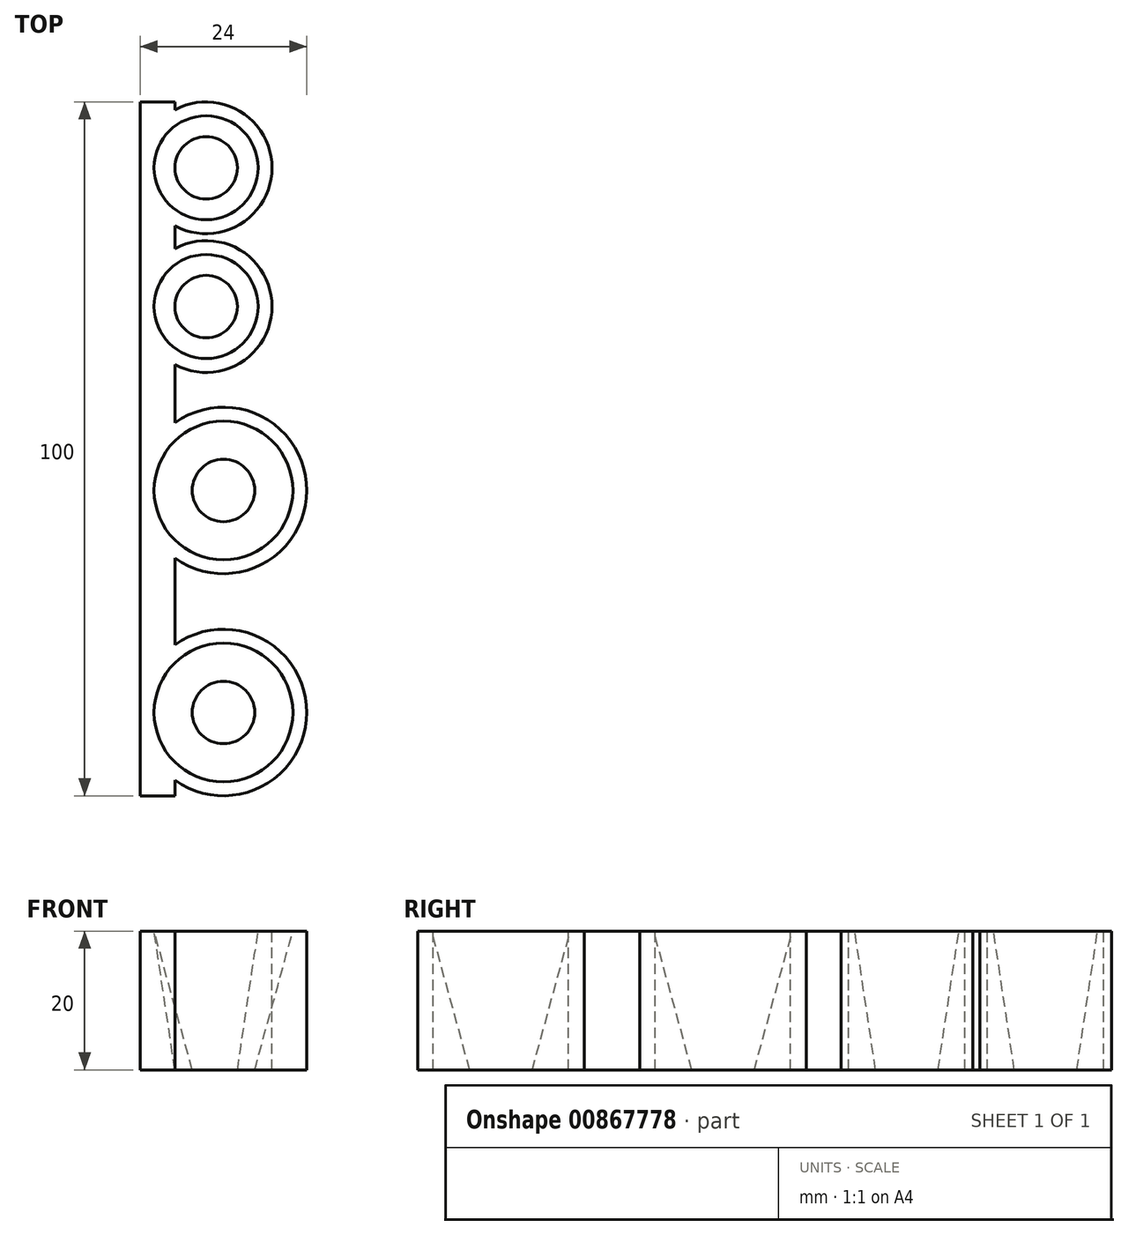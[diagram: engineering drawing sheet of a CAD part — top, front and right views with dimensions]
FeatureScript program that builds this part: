
annotation { "Feature Type Name" : "Feature", "Feature Type Description" : "" }
export const myFeature = defineFeature(function(context is Context, id is Id, definition is map)
    precondition{}
    {
        {
            var Q0;
            Q0=qCreatedBy(makeId("Right.planeOp"),FACE);
            var sketch = newSketch(context, id + "F0", { "sketchPlane" : qUnion([Q0])});
            skLineSegment(sketch, "E0.bottom", {"start": v(50, -10) * mm, "end": v(-50, -10) * mm});
            skLineSegment(sketch, "E0.top", {"start": v(50, 10) * mm, "end": v(-50, 10) * mm});
            skLineSegment(sketch, "E0.left", {"start": v(50, -10) * mm, "end": v(50, 10) * mm});
            skLineSegment(sketch, "E0.right", {"start": v(-50, -10) * mm, "end": v(-50, 10) * mm});
            skPoint(sketch, "E0.middle", {"position": v(0, 0) * mm});
            skSolve(sketch);
        }
        {
            var Q0;
            Q0=makeQuery(id+"F0.imprint","IMPRINT",FACE,{"disambiguationData":[TD([[makeQuery(id+"F0.imprint","IMPRINT",EDGE,{"derivedFrom":sQuery(id+"F0.wireOp",EDGE,"E0.bottom")}),-1.0]])]});
            extrude(context, id + "F1", {"entities" : qUnion([Q0]), "endBound" : BoundingType.SYMMETRIC, "depth" : 25 * mm, "offsetDistance" : 25 * mm});
        }
        {
            var Q0;
            Q0=makeQuery(id+"F1.opExtrude","SWEPT_FACE",FACE,{"disambiguationData":[OSD([sQuery(id+"F0.wireOp",EDGE,"E0.top")])]});
            var sketch = newSketch(context, id + "F2", { "sketchPlane" : qUnion([Q0])});
            skLineSegment(sketch, "E1", {"start": v(-12.5, -50) * mm, "end": v(11.5, -50) * mm});
            skCircle(sketch, "E2", {"center": v(-0.5, -38) * mm, "radius": 12 * mm});
            skPoint(sketch, "E2.centerSnap0", {"position": v(-0.5, -50) * mm});
            skCircle(sketch, "E3", {"center": v(-0.5, -6) * mm, "radius": 10 * mm});
            skCircle(sketch, "E4", {"center": v(-0.5, -38) * mm, "radius": 10 * mm});
            skCircle(sketch, "E5", {"center": v(-0.5, -6) * mm, "radius": 12 * mm});
            skLineSegment(sketch, "E6", {"start": v(-12.5, 50) * mm, "end": v(-3, 50) * mm});
            skCircle(sketch, "E7", {"center": v(-3, 40.5) * mm, "radius": 9.5 * mm});
            skCircle(sketch, "E8", {"center": v(-3, 40.5) * mm, "radius": 7.5 * mm});
            skCircle(sketch, "E9", {"center": v(-3, 20.5) * mm, "radius": 9.5 * mm});
            skCircle(sketch, "E10", {"center": v(-3, 20.5) * mm, "radius": 7.5 * mm});
            skLineSegment(sketch, "E11", {"start": v(-7.5, -50) * mm, "end": v(-7.5, -47.75) * mm});
            skLineSegment(sketch, "E12.trimOffspring", {"start": v(-7.5, -28.25) * mm, "end": v(-7.5, -15.75) * mm});
            skLineSegment(sketch, "E13.trimOffspring", {"start": v(-7.5, 3.75) * mm, "end": v(-7.5, 12.13) * mm});
            skLineSegment(sketch, "E14.trimOffspring", {"start": v(-7.5, 28.87) * mm, "end": v(-7.5, 32.13) * mm});
            skLineSegment(sketch, "E15.trimOffspring", {"start": v(-7.5, 48.87) * mm, "end": v(-7.5, 50) * mm});
            skSolve(sketch);
        }
        {
            var Q0;
            Q0=makeQuery(id+"F1.opExtrude","SWEPT_FACE",FACE,{"disambiguationData":[OSD([sQuery(id+"F0.wireOp",EDGE,"E0.bottom")])]});
            var sketch = newSketch(context, id + "F3", { "sketchPlane" : qUnion([Q0])});
            skLineSegment(sketch, "E16", {"start": v(-12.5, 50) * mm, "end": v(-0.5, 50) * mm});
            skCircle(sketch, "E17", {"center": v(-0.5, 38) * mm, "radius": 6.5 * mm});
            skCircle(sketch, "E18", {"center": v(-0.5, 38) * mm, "radius": 4.5 * mm});
            skCircle(sketch, "E19.0.1.0", {"center": v(-0.5, 6) * mm, "radius": 6.5 * mm});
            skCircle(sketch, "E19.0.1.1", {"center": v(-0.5, 6) * mm, "radius": 4.5 * mm});
            skLineSegment(sketch, "E19.direction1", {"start": v(-0.5, 38) * mm, "end": v(37, 38) * mm, "construction": true});
            skLineSegment(sketch, "E19.direction2", {"start": v(-0.5, 38) * mm, "end": v(-0.5, 6) * mm, "construction": true});
            skLineSegment(sketch, "E20", {"start": v(-12.5, -50) * mm, "end": v(-3, -50) * mm});
            skCircle(sketch, "E21", {"center": v(-3, -40.5) * mm, "radius": 4.5 * mm});
            skCircle(sketch, "E22", {"center": v(-3, -40.5) * mm, "radius": 6.5 * mm});
            skCircle(sketch, "E23.0.1.0", {"center": v(-3, -20.5) * mm, "radius": 6.5 * mm});
            skCircle(sketch, "E23.0.1.1", {"center": v(-3, -20.5) * mm, "radius": 4.5 * mm});
            skLineSegment(sketch, "E23.direction1", {"start": v(-3, -40.5) * mm, "end": v(34.5, -40.5) * mm, "construction": true});
            skLineSegment(sketch, "E23.direction2", {"start": v(-3, -40.5) * mm, "end": v(-3, -20.5) * mm, "construction": true});
            skLineSegment(sketch, "E24", {"start": v(-4.5, 50) * mm, "end": v(-4.5, 43.12) * mm});
            skLineSegment(sketch, "E25.trimOffspring", {"start": v(-4.5, -46.82) * mm, "end": v(-4.5, -50) * mm});
            skLineSegment(sketch, "E26.trimOffspring", {"start": v(-4.5, -26.82) * mm, "end": v(-4.5, -34.18) * mm});
            skLineSegment(sketch, "E27.trimOffspring", {"start": v(-4.5, 0.88) * mm, "end": v(-4.5, -14.18) * mm});
            skLineSegment(sketch, "E28.trimOffspring", {"start": v(-4.5, 32.88) * mm, "end": v(-4.5, 11.12) * mm});
            skSolve(sketch);
        }
        {
            var Q1;
            {var subQ0=sQuery(id+"F2.wireOp",EDGE,"E4");var subQ1=makeQuery(id+"F1.opExtrude","CAP_EDGE",EDGE,{"disambiguationData":[OSD([sQuery(id+"F0.wireOp",EDGE,"E0.top")])],"isStart":false});var subQ2=makeQuery(id+"F2.imprint","INTERSECT",VERTEX,{"disambiguationData":[OD(0.0)],"derivedFrom":[subQ1,subQ0]});Q1=makeQuery(id+"F2.imprint","IMPRINT",FACE,{"disambiguationData":[TD([[makeQuery(id+"F2.imprint","IMPRINT",EDGE,{"disambiguationData":[TD([[subQ2,-1.0]])],"derivedFrom":subQ0}),1.0]])]});}
            var Q2;
            {var subQ0=sQuery(id+"F3.wireOp",EDGE,"E18");var subQ1=makeQuery(id+"F1.opExtrude","CAP_EDGE",EDGE,{"disambiguationData":[OSD([sQuery(id+"F0.wireOp",EDGE,"E0.bottom")])],"isStart":false});var subQ2=makeQuery(id+"F3.imprint","INTERSECT",VERTEX,{"disambiguationData":[OD(0.0)],"derivedFrom":[subQ1,subQ0]});Q2=makeQuery(id+"F3.imprint","IMPRINT",FACE,{"disambiguationData":[TD([[makeQuery(id+"F3.imprint","IMPRINT",EDGE,{"disambiguationData":[TD([[subQ2,-1.0]])],"derivedFrom":subQ0}),1.0]])]});}
            loft(context, id + "F4", {"operationType" : NewBodyOperationType.REMOVE, "sheetProfilesArray" : [{ "sheetProfileEntities" : qUnion([Q1]) }, { "sheetProfileEntities" : qUnion([Q2]) }]});
        }
        {
            var Q1;
            {var subQ0=sQuery(id+"F2.wireOp",EDGE,"E3");var subQ1=makeQuery(id+"F1.opExtrude","CAP_EDGE",EDGE,{"disambiguationData":[OSD([sQuery(id+"F0.wireOp",EDGE,"E0.top")])],"isStart":false});var subQ2=makeQuery(id+"F2.imprint","INTERSECT",VERTEX,{"disambiguationData":[OD(0.0)],"derivedFrom":[subQ1,subQ0]});Q1=makeQuery(id+"F2.imprint","IMPRINT",FACE,{"disambiguationData":[TD([[makeQuery(id+"F2.imprint","IMPRINT",EDGE,{"disambiguationData":[TD([[subQ2,-1.0]])],"derivedFrom":subQ0}),1.0]])]});}
            var Q2;
            {var subQ0=sQuery(id+"F3.wireOp",EDGE,"E19.0.1.1");var subQ1=makeQuery(id+"F1.opExtrude","CAP_EDGE",EDGE,{"disambiguationData":[OSD([sQuery(id+"F0.wireOp",EDGE,"E0.bottom")])],"isStart":false});var subQ2=makeQuery(id+"F3.imprint","INTERSECT",VERTEX,{"disambiguationData":[OD(0.0)],"derivedFrom":[subQ1,subQ0]});Q2=makeQuery(id+"F3.imprint","IMPRINT",FACE,{"disambiguationData":[TD([[makeQuery(id+"F3.imprint","IMPRINT",EDGE,{"disambiguationData":[TD([[subQ2,-1.0]])],"derivedFrom":subQ0}),1.0]])]});}
            loft(context, id + "F5", {"operationType" : NewBodyOperationType.REMOVE, "sheetProfilesArray" : [{ "sheetProfileEntities" : qUnion([Q1]) }, { "sheetProfileEntities" : qUnion([Q2]) }]});
        }
        {
            var Q1;
            {var subQ0=sQuery(id+"F2.wireOp",EDGE,"E10");var subQ1=makeQuery(id+"F1.opExtrude","CAP_EDGE",EDGE,{"disambiguationData":[OSD([sQuery(id+"F0.wireOp",EDGE,"E0.top")])],"isStart":false});var subQ2=makeQuery(id+"F2.imprint","INTERSECT",VERTEX,{"disambiguationData":[OD(0.0)],"derivedFrom":[subQ1,subQ0]});Q1=makeQuery(id+"F2.imprint","IMPRINT",FACE,{"disambiguationData":[TD([[makeQuery(id+"F2.imprint","IMPRINT",EDGE,{"disambiguationData":[TD([[subQ2,-1.0]])],"derivedFrom":subQ0}),1.0]])]});}
            var Q2;
            {var subQ0=sQuery(id+"F3.wireOp",EDGE,"E23.0.1.1");var subQ1=makeQuery(id+"F1.opExtrude","CAP_EDGE",EDGE,{"disambiguationData":[OSD([sQuery(id+"F0.wireOp",EDGE,"E0.bottom")])],"isStart":false});var subQ2=makeQuery(id+"F3.imprint","INTERSECT",VERTEX,{"disambiguationData":[OD(0.0)],"derivedFrom":[subQ1,subQ0]});Q2=makeQuery(id+"F3.imprint","IMPRINT",FACE,{"disambiguationData":[TD([[makeQuery(id+"F3.imprint","IMPRINT",EDGE,{"disambiguationData":[TD([[subQ2,1.0]])],"derivedFrom":subQ0}),1.0]])]});}
            loft(context, id + "F6", {"operationType" : NewBodyOperationType.REMOVE, "sheetProfilesArray" : [{ "sheetProfileEntities" : qUnion([Q1]) }, { "sheetProfileEntities" : qUnion([Q2]) }]});
        }
        {
            var Q1;
            {var subQ0=sQuery(id+"F2.wireOp",EDGE,"E8");var subQ1=makeQuery(id+"F1.opExtrude","CAP_EDGE",EDGE,{"disambiguationData":[OSD([sQuery(id+"F0.wireOp",EDGE,"E0.top")])],"isStart":false});var subQ2=makeQuery(id+"F2.imprint","INTERSECT",VERTEX,{"disambiguationData":[OD(0.0)],"derivedFrom":[subQ1,subQ0]});Q1=makeQuery(id+"F2.imprint","IMPRINT",FACE,{"disambiguationData":[TD([[makeQuery(id+"F2.imprint","IMPRINT",EDGE,{"disambiguationData":[TD([[subQ2,1.0]])],"derivedFrom":subQ0}),1.0]])]});}
            var Q2;
            {var subQ0=sQuery(id+"F3.wireOp",EDGE,"E21");var subQ1=makeQuery(id+"F1.opExtrude","CAP_EDGE",EDGE,{"disambiguationData":[OSD([sQuery(id+"F0.wireOp",EDGE,"E0.bottom")])],"isStart":false});var subQ2=makeQuery(id+"F3.imprint","INTERSECT",VERTEX,{"disambiguationData":[OD(0.0)],"derivedFrom":[subQ1,subQ0]});Q2=makeQuery(id+"F3.imprint","IMPRINT",FACE,{"disambiguationData":[TD([[makeQuery(id+"F3.imprint","IMPRINT",EDGE,{"disambiguationData":[TD([[subQ2,1.0]])],"derivedFrom":subQ0}),1.0]])]});}
            loft(context, id + "F7", {"operationType" : NewBodyOperationType.REMOVE, "sheetProfilesArray" : [{ "sheetProfileEntities" : qUnion([Q1]) }, { "sheetProfileEntities" : qUnion([Q2]) }]});
        }
        {
            var Q0;
            {var subQ5=sQuery(id+"F2.wireOp",EDGE,"E12.trimOffspring");Q0=makeQuery(id+"F2.imprint","IMPRINT",FACE,{"disambiguationData":[TD([[makeQuery(id+"F2.imprint","IMPRINT",EDGE,{"derivedFrom":subQ5}),-1.0]])]});}
            var Q1;
            {var subQ0=sQuery(id+"F2.wireOp",EDGE,"E11");Q1=makeQuery(id+"F2.imprint","IMPRINT",FACE,{"disambiguationData":[TD([[makeQuery(id+"F2.imprint","IMPRINT",EDGE,{"derivedFrom":subQ0}),-1.0]])]});}
            var Q2;
            {var subQ3=sQuery(id+"F2.wireOp",EDGE,"E15.trimOffspring");Q2=makeQuery(id+"F2.imprint","IMPRINT",FACE,{"disambiguationData":[TD([[makeQuery(id+"F2.imprint","IMPRINT",EDGE,{"derivedFrom":subQ3}),-1.0]])]});}
            extrude(context, id + "F8", {"entities" : qUnion([Q0, Q1, Q2]), "operationType" : NewBodyOperationType.REMOVE, "oppositeDirection" : true, "depth" : 25 * mm, "offsetDistance" : 25 * mm});
        }
    });
